# Revit family: Haworth_Pergola_Panel_TopRail_Radial
name_source: partatom
category: Furniture Systems
revit_build: Autodesk Revit 2018 (Build: 20170223_1515(x64)
units: mm (PartAtom-declared; Revit-internal decimal feet)

## family parameters
Always vertical = Yes
Cut with Voids When Loaded = No
OmniClass Number = 23.40.70.14.64.21
OmniClass Title = Systems Furniture
Part Type = Normal
Room Calculation Point = No
Round Connector Dimension = Use Diameter
Shared = No
Work Plane-Based = No

## types (1)
- 72 in. radius
    Actual Depth = 4"
    Actual Height = 4 25/128"
    Assembly Code = E2020200
    Description = Haworth - Pergola Panel - Top Rail - Radial
    Manufacturer = Haworth
    Max. Height = 4"
    Max. Width = 144"
    Min. Height = 4"
    Min. Width = 48"
    Model = Haworth Pergola
    Revision Number = 1
    Size = Verify Final Dim. w/ Haworth
    Standard Radius = 72 in.
    Sustainability Info = http://www.haworth.com
    Trim Finish = Haworth _ Paint _ Undecided _ Pergola
    URL = http://www.haworth.com
    URL - Product = https://www.haworth.com
    Warranty = http://www.haworth.com

## geometry (parser evidence)
native form markers: Sweep x3
no freeform markers — native parametric forms only
